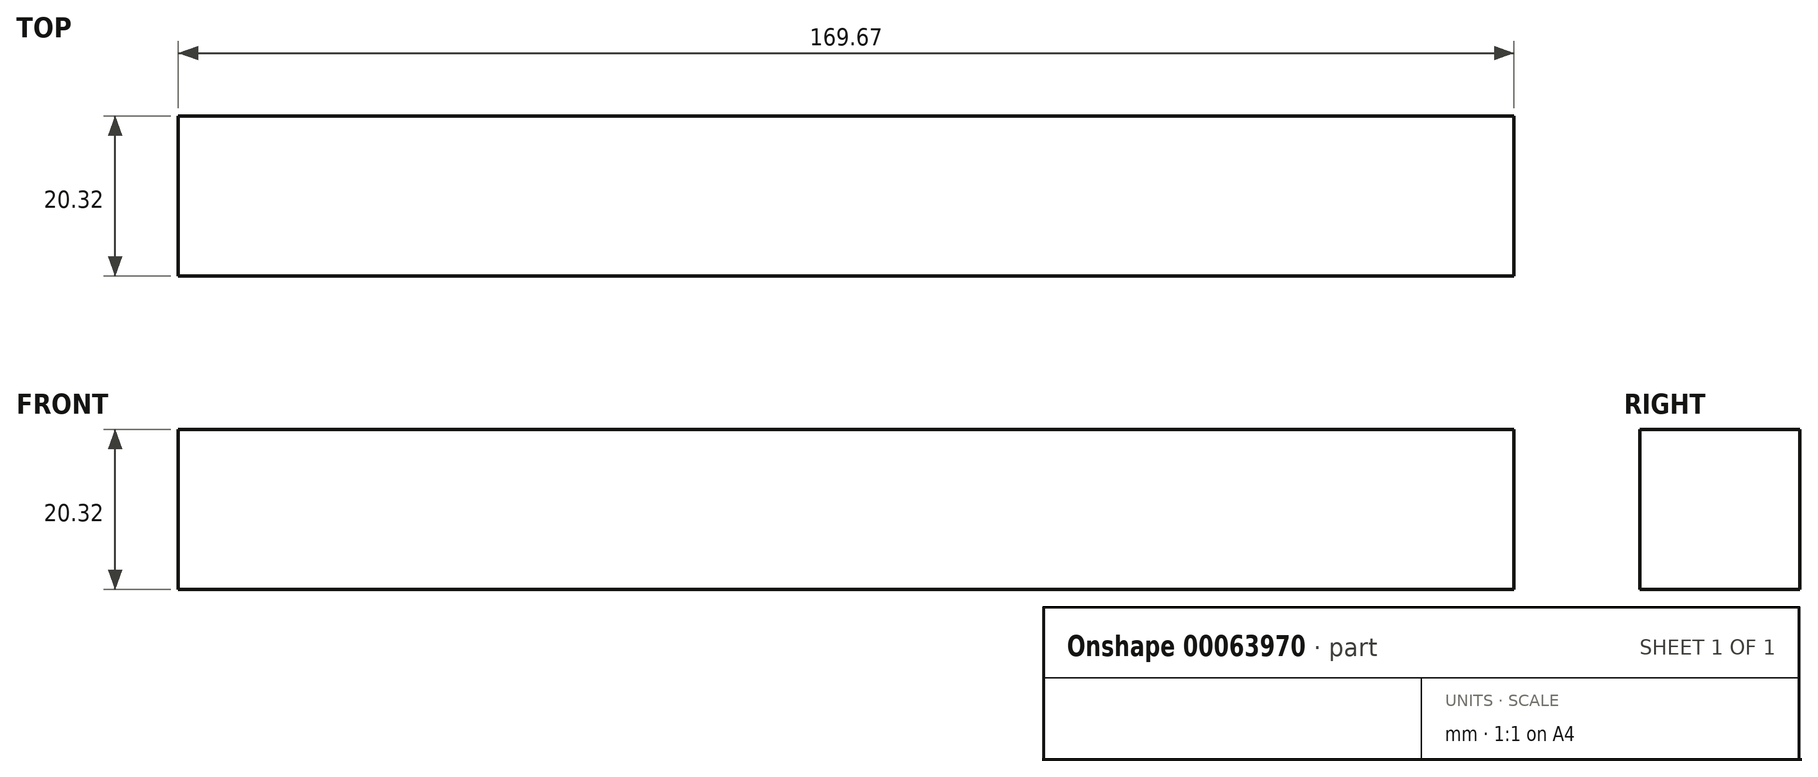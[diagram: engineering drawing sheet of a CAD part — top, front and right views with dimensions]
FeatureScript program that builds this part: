
annotation { "Feature Type Name" : "Feature", "Feature Type Description" : "" }
export const myFeature = defineFeature(function(context is Context, id is Id, definition is map)
    precondition{}
    {
        {
            var Q0;
            Q0=qCreatedBy(makeId("Front.planeOp"),FACE);
            var sketch = newSketch(context, id + "F0", { "sketchPlane" : qUnion([Q0])});
            skLineSegment(sketch, "E0.bottom", {"start": v(-82.03, 24.12) * mm, "end": v(87.64, 24.12) * mm});
            skLineSegment(sketch, "E0.top", {"start": v(-82.03, 3.8) * mm, "end": v(87.64, 3.8) * mm});
            skLineSegment(sketch, "E0.left", {"start": v(-82.03, 24.12) * mm, "end": v(-82.03, 3.8) * mm});
            skLineSegment(sketch, "E0.right", {"start": v(87.64, 24.12) * mm, "end": v(87.64, 3.8) * mm});
            skSolve(sketch);
        }
        {
            var Q0;
            Q0 = qSketchRegion(id + "F0", true);
            extrude(context, id + "F1", {"entities" : qUnion([Q0]), "depth" : 20.32 * mm});
        }
    });
